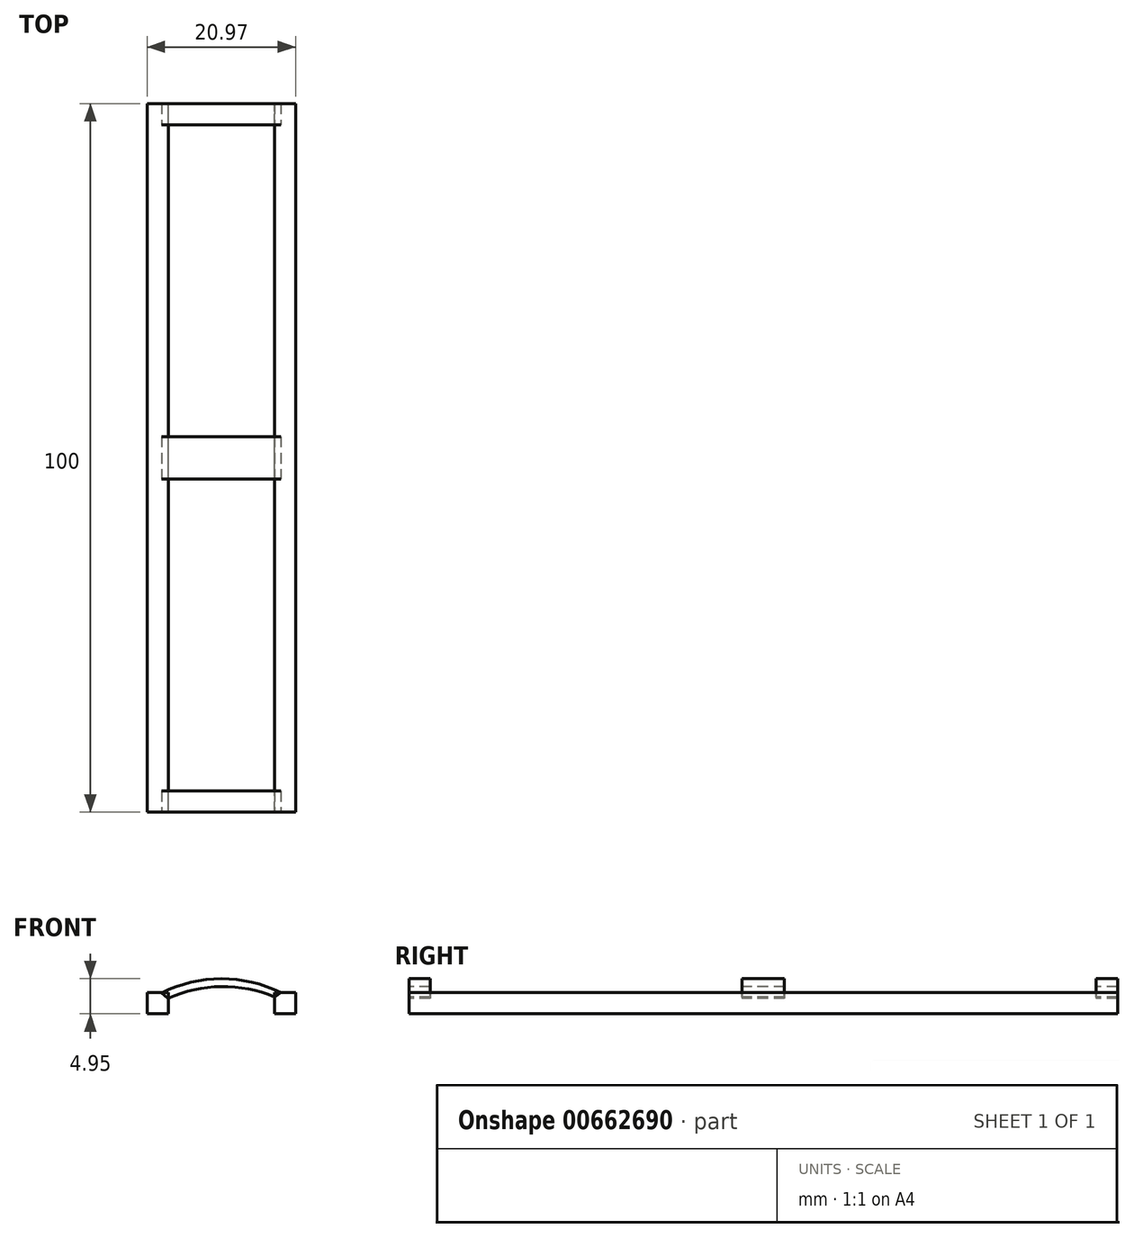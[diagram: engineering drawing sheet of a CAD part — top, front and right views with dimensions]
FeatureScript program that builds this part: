
annotation { "Feature Type Name" : "Feature", "Feature Type Description" : "" }
export const myFeature = defineFeature(function(context is Context, id is Id, definition is map)
    precondition{}
    {
        {
            var Q0;
            Q0=qCreatedBy(makeId("Top.planeOp"),FACE);
            var sketch = newSketch(context, id + "F0", { "sketchPlane" : qUnion([Q0])});
            skLineSegment(sketch, "E0.bottom", {"start": v(0, 0) * mm, "end": v(3, 0) * mm});
            skLineSegment(sketch, "E0.top", {"start": v(0, 100) * mm, "end": v(3, 100) * mm});
            skLineSegment(sketch, "E0.left", {"start": v(0, 0) * mm, "end": v(0, 100) * mm});
            skLineSegment(sketch, "E0.right", {"start": v(3, 0) * mm, "end": v(3, 100) * mm});
            skLineSegment(sketch, "E1.bottom", {"start": v(17.97, 0) * mm, "end": v(20.97, 0) * mm});
            skLineSegment(sketch, "E1.top", {"start": v(17.97, 100) * mm, "end": v(20.97, 100) * mm});
            skLineSegment(sketch, "E1.left", {"start": v(17.97, 0) * mm, "end": v(17.97, 100) * mm});
            skLineSegment(sketch, "E1.right", {"start": v(20.97, 0) * mm, "end": v(20.97, 100) * mm});
            skSolve(sketch);
        }
        {
            var Q0;
            Q0 = qSketchRegion(id + "F0", true);
            extrude(context, id + "F1", {"entities" : qUnion([Q0]), "depth" : 3 * mm, "offsetDistance" : 25 * mm});
        }
        {
            var Q0;
            Q0=qCreatedBy(makeId("Front.planeOp"),FACE);
            var sketch = newSketch(context, id + "F2", { "sketchPlane" : qUnion([Q0])});
            skArc(sketch, "E2", {"start": v(18, 2.37) * mm, "mid": v(10.47, 3.86) * mm, "end": v(2.98, 2.2) * mm});
            skArc(sketch, "E3", {"start": v(18.89, 2.98) * mm, "mid": v(10.49, 4.95) * mm, "end": v(2.09, 2.97) * mm});
            skLineSegment(sketch, "E4", {"start": v(2.09, 2.97) * mm, "end": v(2.98, 2.2) * mm});
            skLineSegment(sketch, "E5", {"start": v(18.89, 2.98) * mm, "end": v(18, 2.37) * mm});
            skSolve(sketch);
        }
        {
            var Q0;
            Q0 = qSketchRegion(id + "F2", true);
            extrude(context, id + "F3", {"entities" : qUnion([Q0]), "oppositeDirection" : true, "depth" : 3 * mm, "offsetDistance" : 25 * mm});
        }
        {
            var Q0;
            Q0=makeQuery(id+"F2.imprint","IMPRINT",FACE,{"disambiguationData":[TD([[makeQuery(id+"F2.imprint","IMPRINT",EDGE,{"derivedFrom":sQuery(id+"F2.wireOp",EDGE,"E2")}),-1.0]])]});
            extrude(context, id + "F4", {"entities" : qUnion([Q0]), "oppositeDirection" : true, "depth" : 53 * mm, "offsetDistance" : 25 * mm, "hasSecondDirection" : true, "secondDirectionOppositeDirection" : true, "secondDirectionDepth" : 47 * mm});
        }
        {
            var Q0;
            Q0=makeQuery(id+"F2.imprint","IMPRINT",FACE,{"disambiguationData":[TD([[makeQuery(id+"F2.imprint","IMPRINT",EDGE,{"derivedFrom":sQuery(id+"F2.wireOp",EDGE,"E2")}),-1.0]])]});
            extrude(context, id + "F5", {"entities" : qUnion([Q0]), "oppositeDirection" : true, "depth" : 100 * mm, "offsetDistance" : 25 * mm, "hasSecondDirection" : true, "secondDirectionOppositeDirection" : true, "secondDirectionDepth" : 97 * mm});
        }
    });
